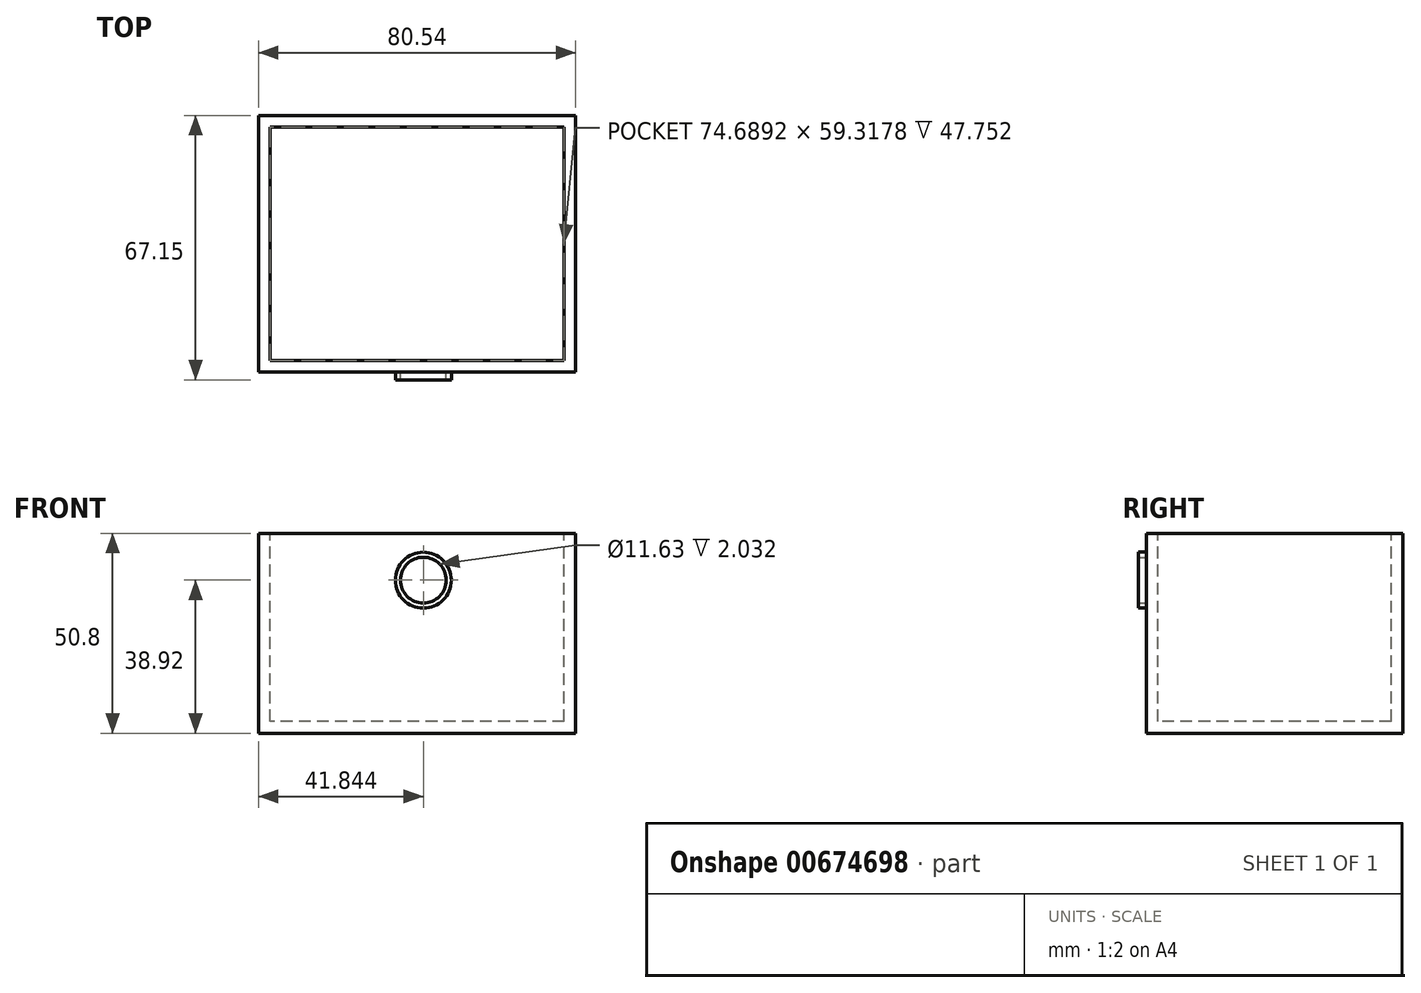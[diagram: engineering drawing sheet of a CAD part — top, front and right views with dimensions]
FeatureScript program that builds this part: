
annotation { "Feature Type Name" : "Feature", "Feature Type Description" : "" }
export const myFeature = defineFeature(function(context is Context, id is Id, definition is map)
    precondition{}
    {
        {
            var Q0;
            Q0=qCreatedBy(makeId("Top.planeOp"),FACE);
            var sketch = newSketch(context, id + "F0", { "sketchPlane" : qUnion([Q0])});
            skLineSegment(sketch, "E0.bottom", {"start": v(40.27, -32.56) * mm, "end": v(-40.27, -32.56) * mm});
            skLineSegment(sketch, "E0.top", {"start": v(40.27, 32.56) * mm, "end": v(-40.27, 32.56) * mm});
            skLineSegment(sketch, "E0.left", {"start": v(40.27, -32.56) * mm, "end": v(40.27, 32.56) * mm});
            skLineSegment(sketch, "E0.right", {"start": v(-40.27, -32.56) * mm, "end": v(-40.27, 32.56) * mm});
            skPoint(sketch, "E0.middle", {"position": v(0, 0) * mm});
            skSolve(sketch);
        }
        {
            var Q0;
            Q0 = qSketchRegion(id + "F0", true);
            extrude(context, id + "F1", {"entities" : qUnion([Q0]), "depth" : 50.8 * mm, "offsetDistance" : 25.4 * mm});
        }
        {
            var Q0;
            Q0=makeQuery(id+"F1.opExtrude","CAP_FACE",FACE,{"disambiguationData":[OSD([sQuery(id+"F0.wireOp",EDGE,"E0.bottom"),sQuery(id+"F0.wireOp",EDGE,"E0.top"),sQuery(id+"F0.wireOp",EDGE,"E0.left"),sQuery(id+"F0.wireOp",EDGE,"E0.right")])],"isStart":false});
            var sketch = newSketch(context, id + "F2", { "sketchPlane" : qUnion([Q0])});
            skLineSegment(sketch, "E1.bottom", {"start": v(37.34, 29.66) * mm, "end": v(-37.34, 29.66) * mm});
            skLineSegment(sketch, "E1.top", {"start": v(37.34, -29.66) * mm, "end": v(-37.34, -29.66) * mm});
            skLineSegment(sketch, "E1.left", {"start": v(37.34, 29.66) * mm, "end": v(37.34, -29.66) * mm});
            skLineSegment(sketch, "E1.right", {"start": v(-37.34, 29.66) * mm, "end": v(-37.34, -29.66) * mm});
            skPoint(sketch, "E1.middle", {"position": v(0, 0) * mm});
            skSolve(sketch);
        }
        {
            var Q0;
            Q0=makeQuery(id+"F2.imprint","IMPRINT",FACE,{"disambiguationData":[TD([[makeQuery(id+"F2.imprint","IMPRINT",EDGE,{"derivedFrom":sQuery(id+"F2.wireOp",EDGE,"E1.bottom")}),1.0]])]});
            extrude(context, id + "F3", {"entities" : qUnion([Q0]), "operationType" : NewBodyOperationType.REMOVE, "oppositeDirection" : true, "depth" : 47.75 * mm, "offsetDistance" : 25.4 * mm});
        }
        {
            var Q0;
            Q0=makeQuery(id+"F1.opExtrude","SWEPT_FACE",FACE,{"disambiguationData":[OSD([sQuery(id+"F0.wireOp",EDGE,"E0.bottom")])]});
            var sketch = newSketch(context, id + "F4", { "sketchPlane" : qUnion([Q0])});
            skCircle(sketch, "E2", {"center": v(1.57, 38.92) * mm, "radius": 7.1 * mm});
            skCircle(sketch, "E3.0", {"center": v(1.57, 38.92) * mm, "radius": 5.81 * mm});
            skSolve(sketch);
        }
        {
            var Q0;
            Q0=makeQuery(id+"F4.imprint","IMPRINT",FACE,{"disambiguationData":[TD([[makeQuery(id+"F4.imprint","IMPRINT",EDGE,{"derivedFrom":sQuery(id+"F4.wireOp",EDGE,"E2")}),1.0]])]});
            extrude(context, id + "F5", {"entities" : qUnion([Q0]), "operationType" : NewBodyOperationType.ADD, "depth" : 2.03 * mm, "offsetDistance" : 25.4 * mm});
        }
    });
